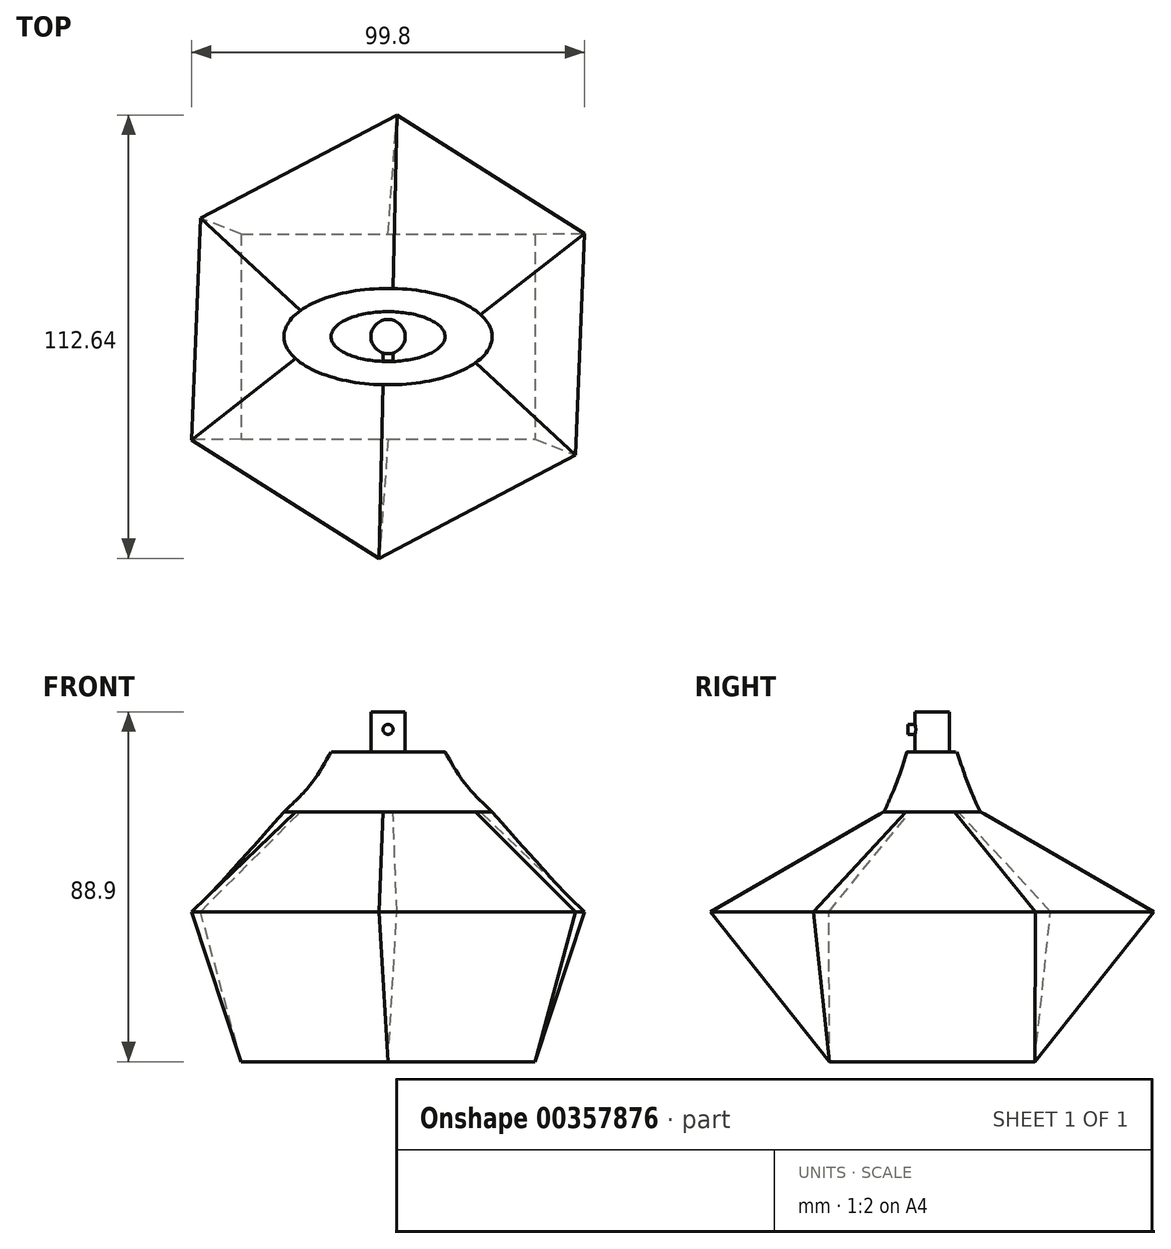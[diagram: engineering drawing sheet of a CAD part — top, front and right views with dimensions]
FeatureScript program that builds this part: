
annotation { "Feature Type Name" : "Feature", "Feature Type Description" : "" }
export const myFeature = defineFeature(function(context is Context, id is Id, definition is map)
    precondition{}
    {
        {
            var Q0;
            Q0=qCreatedBy(makeId("Top.planeOp"),FACE);
            var sketch = newSketch(context, id + "F0", { "sketchPlane" : qUnion([Q0])});
            skLineSegment(sketch, "E0.bottom", {"start": v(-37.29, 26.07) * mm, "end": v(37.29, 26.07) * mm});
            skLineSegment(sketch, "E0.top", {"start": v(-37.29, -26.07) * mm, "end": v(37.29, -26.07) * mm});
            skLineSegment(sketch, "E0.left", {"start": v(-37.29, 26.07) * mm, "end": v(-37.29, -26.07) * mm});
            skLineSegment(sketch, "E0.right", {"start": v(37.29, 26.07) * mm, "end": v(37.29, -26.07) * mm});
            skPoint(sketch, "E0.middle", {"position": v(0, 0) * mm});
            skSolve(sketch);
        }
        {
            var Q0;
            Q0=qCreatedBy(makeId("Top.planeOp"),FACE);
            cPlane(context, id + "F1", {"entities" : qUnion([Q0]), "cplaneType" : CPlaneType.OFFSET, "offset" : 38.1 * mm, "width" : 152.4 * mm, "height" : 152.4 * mm});
        }
        {
            var Q0;
            Q0=qCreatedBy(id+"F1.planeOp",FACE);
            var sketch = newSketch(context, id + "F2", { "sketchPlane" : qUnion([Q0])});
            skCircle(sketch, "E1.cCircle", {"center": v(0, 0) * mm, "radius": 48.81 * mm, "construction": true});
            skLineSegment(sketch, "E1.0", {"start": v(2.24, 56.32) * mm, "end": v(49.9, 26.22) * mm});
            skLineSegment(sketch, "E1.1", {"start": v(49.9, 26.22) * mm, "end": v(47.66, -30.1) * mm});
            skLineSegment(sketch, "E1.2", {"start": v(47.66, -30.1) * mm, "end": v(-2.24, -56.32) * mm});
            skLineSegment(sketch, "E1.3", {"start": v(-2.24, -56.32) * mm, "end": v(-49.9, -26.22) * mm});
            skLineSegment(sketch, "E1.4", {"start": v(-49.9, -26.22) * mm, "end": v(-47.66, 30.1) * mm});
            skLineSegment(sketch, "E1.5", {"start": v(-47.66, 30.1) * mm, "end": v(2.24, 56.32) * mm});
            skPoint(sketch, "E1.0.midPoint", {"position": v(26.07, 41.27) * mm});
            skSolve(sketch);
        }
        {
            var Q0;
            Q0=qCreatedBy(makeId("Top.planeOp"),FACE);
            cPlane(context, id + "F3", {"entities" : qUnion([Q0]), "cplaneType" : CPlaneType.OFFSET, "offset" : 63.5 * mm, "width" : 152.4 * mm, "height" : 152.4 * mm});
        }
        {
            var Q0;
            Q0=qCreatedBy(id+"F3.planeOp",FACE);
            var sketch = newSketch(context, id + "F4", { "sketchPlane" : qUnion([Q0])});
            skEllipse(sketch, "E2", {"center": v(0, 0) * mm, "majorRadius": 26.43 * mm, "minorRadius": 12.24 * mm, "majorAxis": v(1, 0)});
            skSolve(sketch);
        }
        {
            var Q0;
            Q0=makeQuery(id+"F0.imprint","IMPRINT",FACE,{"disambiguationData":[TD([[makeQuery(id+"F0.imprint","IMPRINT",EDGE,{"derivedFrom":sQuery(id+"F0.wireOp",EDGE,"E0.bottom")}),-1.0]])]});
            var Q1;
            Q1=makeQuery(id+"F2.imprint","IMPRINT",FACE,{"disambiguationData":[TD([[makeQuery(id+"F2.imprint","IMPRINT",EDGE,{"derivedFrom":sQuery(id+"F2.wireOp",EDGE,"E1.0")}),-1.0]])]});
            loft(context, id + "F5", {"sheetProfilesArray" : [{ "sheetProfileEntities" : qUnion([Q0]) }, { "sheetProfileEntities" : qUnion([Q1]) }]});
        }
        {
            var Q1;
            Q1=makeQuery(id+"F5.opLoft","CAP_FACE",FACE,{"disambiguationData":[OSD([makeQuery(id+"F2.imprint","IMPRINT",FACE,{"disambiguationData":[TD([[makeQuery(id+"F2.imprint","IMPRINT",EDGE,{"derivedFrom":sQuery(id+"F2.wireOp",EDGE,"E1.0")}),-1.0]])]})])],"isStart":true});
            var Q2;
            Q2=makeQuery(id+"F4.imprint","IMPRINT",FACE,{"disambiguationData":[TD([[makeQuery(id+"F4.imprint","IMPRINT",EDGE,{"derivedFrom":sQuery(id+"F4.wireOp",EDGE,"E2")}),1.0]])]});
            loft(context, id + "F6", {"operationType" : NewBodyOperationType.ADD, "sheetProfilesArray" : [{ "sheetProfileEntities" : qUnion([Q1]) }, { "sheetProfileEntities" : qUnion([Q2]) }]});
        }
        {
            var Q0;
            Q0=qCreatedBy(makeId("Top.planeOp"),FACE);
            cPlane(context, id + "F7", {"entities" : qUnion([Q0]), "cplaneType" : CPlaneType.OFFSET, "offset" : 78.74 * mm, "width" : 150 * mm, "height" : 150 * mm});
        }
        {
            var Q0;
            Q0=qCreatedBy(id+"F7.planeOp",FACE);
            var sketch = newSketch(context, id + "F8", { "sketchPlane" : qUnion([Q0])});
            skEllipse(sketch, "E3", {"center": v(0, 0) * mm, "majorRadius": 14.48 * mm, "minorRadius": 6.34 * mm, "majorAxis": v(-1, 0)});
            skSolve(sketch);
        }
        {
            var Q0;
            Q0=qCreatedBy(makeId("Top.planeOp"),FACE);
            cPlane(context, id + "F9", {"entities" : qUnion([Q0]), "cplaneType" : CPlaneType.OFFSET, "offset" : 71.12 * mm, "width" : 152.4 * mm, "height" : 152.4 * mm});
        }
        {
            var Q0;
            Q0=qCreatedBy(id+"F9.planeOp",FACE);
            var sketch = newSketch(context, id + "F10", { "sketchPlane" : qUnion([Q0])});
            skEllipse(sketch, "E4", {"center": v(0, 0) * mm, "majorRadius": 19.19 * mm, "minorRadius": 8.92 * mm, "majorAxis": v(-1, 0)});
            skSolve(sketch);
        }
        {
            var Q1;
            Q1=makeQuery(id+"F6.opLoft","CAP_FACE",FACE,{"disambiguationData":[OSD([makeQuery(id+"F4.imprint","IMPRINT",FACE,{"disambiguationData":[TD([[makeQuery(id+"F4.imprint","IMPRINT",EDGE,{"derivedFrom":sQuery(id+"F4.wireOp",EDGE,"E2")}),1.0]])]})])],"isStart":true});
            var Q2;
            Q2=makeQuery(id+"F10.imprint","IMPRINT",FACE,{"disambiguationData":[TD([[makeQuery(id+"F10.imprint","IMPRINT",EDGE,{"derivedFrom":sQuery(id+"F10.wireOp",EDGE,"E4")}),1.0]])]});
            var Q3;
            Q3=makeQuery(id+"F8.imprint","IMPRINT",FACE,{"disambiguationData":[TD([[makeQuery(id+"F8.imprint","IMPRINT",EDGE,{"derivedFrom":sQuery(id+"F8.wireOp",EDGE,"E3")}),1.0]])]});
            loft(context, id + "F11", {"operationType" : NewBodyOperationType.ADD, "sheetProfilesArray" : [{ "sheetProfileEntities" : qUnion([Q1]) }, { "sheetProfileEntities" : qUnion([Q2]) }, { "sheetProfileEntities" : qUnion([Q3]) }]});
        }
        {
            var Q0;
            Q0=qCreatedBy(makeId("Top.planeOp"),FACE);
            cPlane(context, id + "F12", {"entities" : qUnion([Q0]), "cplaneType" : CPlaneType.OFFSET, "offset" : 88.9 * mm, "width" : 150 * mm, "height" : 150 * mm});
        }
        {
            var Q0;
            Q0=qCreatedBy(id+"F12.planeOp",FACE);
            var sketch = newSketch(context, id + "F13", { "sketchPlane" : qUnion([Q0])});
            skCircle(sketch, "E5", {"center": v(0, 0) * mm, "radius": 4.35 * mm});
            skSolve(sketch);
        }
        {
            var Q0;
            Q0=makeQuery(id+"F13.imprint","IMPRINT",FACE,{"disambiguationData":[TD([[makeQuery(id+"F13.imprint","IMPRINT",EDGE,{"derivedFrom":sQuery(id+"F13.wireOp",EDGE,"E5")}),1.0]])]});
            extrude(context, id + "F14", {"entities" : qUnion([Q0]), "operationType" : NewBodyOperationType.ADD, "oppositeDirection" : true, "depth" : 10.67 * mm});
        }
        {
            var Q0;
            Q0=qCreatedBy(makeId("Front.planeOp"),FACE);
            var sketch = newSketch(context, id + "F15", { "sketchPlane" : qUnion([Q0])});
            skCircle(sketch, "E6", {"center": v(0, 84.42) * mm, "radius": 1.27 * mm});
            skSolve(sketch);
        }
        {
            var Q0;
            Q0 = qSketchRegion(id + "F15", true);
            extrude(context, id + "F16", {"entities" : qUnion([Q0]), "operationType" : NewBodyOperationType.ADD, "depth" : 6.2 * mm});
        }
    });
